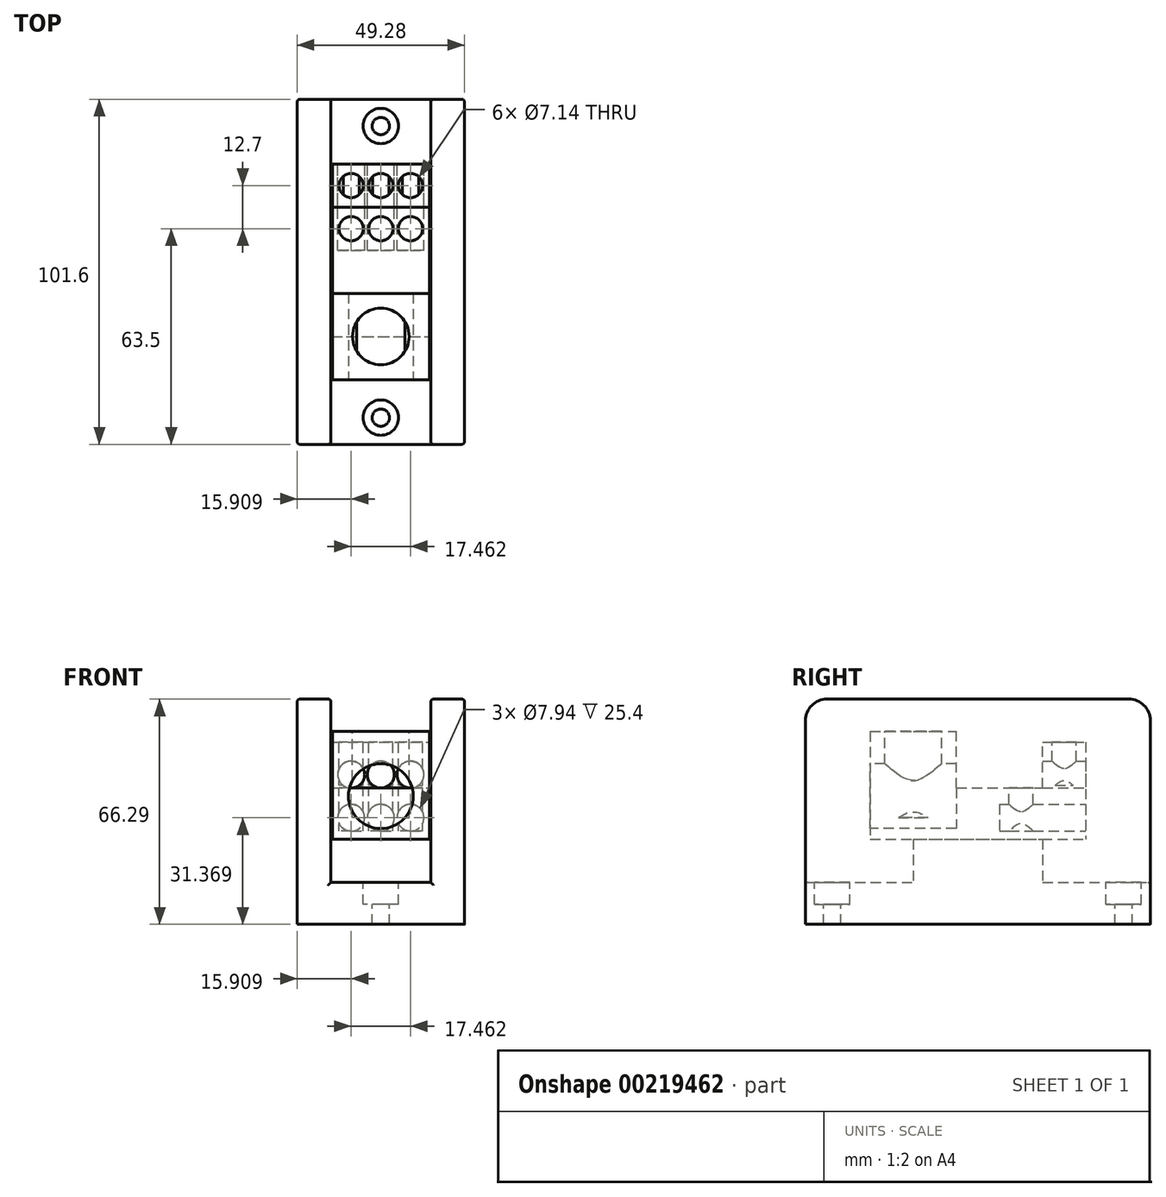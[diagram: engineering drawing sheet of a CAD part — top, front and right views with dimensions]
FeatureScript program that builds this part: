
annotation { "Feature Type Name" : "Feature", "Feature Type Description" : "" }
export const myFeature = defineFeature(function(context is Context, id is Id, definition is map)
    precondition{}
    {
        {
            var Q0;
            Q0=qCreatedBy(makeId("Top.planeOp"),FACE);
            var sketch = newSketch(context, id + "F0", { "sketchPlane" : qUnion([Q0])});
            skLineSegment(sketch, "E0.bottom", {"start": v(-24.64, -50.8) * mm, "end": v(24.64, -50.8) * mm});
            skLineSegment(sketch, "E0.top", {"start": v(-24.64, 50.8) * mm, "end": v(24.64, 50.8) * mm});
            skLineSegment(sketch, "E0.left", {"start": v(-24.64, -50.8) * mm, "end": v(-24.64, 50.8) * mm});
            skLineSegment(sketch, "E0.right", {"start": v(24.64, -50.8) * mm, "end": v(24.64, 50.8) * mm});
            skPoint(sketch, "E0.middle", {"position": v(0, 0) * mm});
            skSolve(sketch);
        }
        {
            var Q0;
            Q0=qSketchRegion(id+"F0",true);
            extrude(context, id + "F1", {"entities" : qUnion([Q0]), "depth" : 66.3 * mm});
        }
        {
            var Q0;
            Q0=makeQuery(id+"F1.opExtrude","CAP_FACE",FACE,{"disambiguationData":[OSD([sQuery(id+"F0.wireOp",EDGE,"E0.bottom"),sQuery(id+"F0.wireOp",EDGE,"E0.top"),sQuery(id+"F0.wireOp",EDGE,"E0.left"),sQuery(id+"F0.wireOp",EDGE,"E0.right")])],"isStart":false});
            var sketch = newSketch(context, id + "F2", { "sketchPlane" : qUnion([Q0])});
            skLineSegment(sketch, "E1.bottom", {"start": v(14.73, -50.8) * mm, "end": v(-14.73, -50.8) * mm});
            skLineSegment(sketch, "E1.top", {"start": v(14.73, 50.8) * mm, "end": v(-14.73, 50.8) * mm});
            skLineSegment(sketch, "E1.left", {"start": v(14.73, -50.8) * mm, "end": v(14.73, 50.8) * mm});
            skLineSegment(sketch, "E1.right", {"start": v(-14.73, -50.8) * mm, "end": v(-14.73, 50.8) * mm});
            skPoint(sketch, "E1.middle", {"position": v(0, 0) * mm});
            skSolve(sketch);
        }
        {
            var Q0;
            Q0=qSketchRegion(id+"F2",true);
            extrude(context, id + "F3", {"entities" : qUnion([Q0]), "operationType" : NewBodyOperationType.REMOVE, "oppositeDirection" : true, "depth" : 53.97 * mm});
        }
        {
            var Q0;
            Q0=makeQuery(id+"F3.boolean.opBoolean","COPY",FACE,{"derivedFrom":makeQuery(id+"F3.opExtrude","CAP_FACE",FACE,{"disambiguationData":[OSD([sQuery(id+"F2.wireOp",EDGE,"E1.bottom"),sQuery(id+"F2.wireOp",EDGE,"E1.top"),sQuery(id+"F2.wireOp",EDGE,"E1.left"),sQuery(id+"F2.wireOp",EDGE,"E1.right")])],"isStart":false})});
            var sketch = newSketch(context, id + "F4", { "sketchPlane" : qUnion([Q0])});
            skPoint(sketch, "E2.middle", {"position": v(0, 42.93) * mm});
            skPoint(sketch, "E3.middle", {"position": v(0, -42.93) * mm});
            skCircle(sketch, "E4", {"center": v(0, 42.93) * mm, "radius": 2.54 * mm});
            skCircle(sketch, "E5", {"center": v(0, -42.93) * mm, "radius": 2.54 * mm});
            skSolve(sketch);
        }
        {
            var Q0;
            Q0=qSketchRegion(id+"F4",true);
            extrude(context, id + "F5", {"entities" : qUnion([Q0]), "operationType" : NewBodyOperationType.REMOVE, "oppositeDirection" : true, "depth" : 12.32 * mm});
        }
        {
            var Q0;
            Q0=makeQuery(id+"F3.boolean.opBoolean","COPY",FACE,{"derivedFrom":makeQuery(id+"F3.opExtrude","CAP_FACE",FACE,{"disambiguationData":[OSD([sQuery(id+"F2.wireOp",EDGE,"E1.bottom"),sQuery(id+"F2.wireOp",EDGE,"E1.top"),sQuery(id+"F2.wireOp",EDGE,"E1.left"),sQuery(id+"F2.wireOp",EDGE,"E1.right")])],"isStart":false})});
            var sketch = newSketch(context, id + "F6", { "sketchPlane" : qUnion([Q0])});
            skCircle(sketch, "E6", {"center": v(0, 42.93) * mm, "radius": 5.2 * mm});
            skCircle(sketch, "E7", {"center": v(0, -42.93) * mm, "radius": 5.2 * mm});
            skSolve(sketch);
        }
        {
            var Q0;
            Q0=qSketchRegion(id+"F6",true);
            extrude(context, id + "F7", {"entities" : qUnion([Q0]), "operationType" : NewBodyOperationType.REMOVE, "oppositeDirection" : true, "depth" : 6.48 * mm});
        }
        {
            var Q0;
            {var subQ0=sQuery(id+"F0.wireOp",EDGE,"E0.left");var subQ1=sQuery(id+"F0.wireOp",EDGE,"E0.top");Q0=makeQuery(id+"F3.boolean.opBoolean","SPLIT",EDGE,{"disambiguationData":[TD([makeQuery(id+"F1.opExtrude","SWEPT_FACE",FACE,{"disambiguationData":[OSD([subQ0])]})])],"derivedFrom":makeQuery(id+"F1.opExtrude","CAP_EDGE",EDGE,{"disambiguationData":[OSD([subQ1])],"isStart":false})});}
            var Q1;
            {var subQ0=sQuery(id+"F0.wireOp",EDGE,"E0.right");var subQ1=sQuery(id+"F0.wireOp",EDGE,"E0.top");Q1=makeQuery(id+"F3.boolean.opBoolean","SPLIT",EDGE,{"disambiguationData":[TD([makeQuery(id+"F1.opExtrude","SWEPT_FACE",FACE,{"disambiguationData":[OSD([subQ0])]})])],"derivedFrom":makeQuery(id+"F1.opExtrude","CAP_EDGE",EDGE,{"disambiguationData":[OSD([subQ1])],"isStart":false})});}
            var Q2;
            {var subQ0=sQuery(id+"F0.wireOp",EDGE,"E0.bottom");var subQ1=sQuery(id+"F0.wireOp",EDGE,"E0.right");Q2=makeQuery(id+"F3.boolean.opBoolean","SPLIT",EDGE,{"disambiguationData":[TD([makeQuery(id+"F1.opExtrude","SWEPT_FACE",FACE,{"disambiguationData":[OSD([subQ1])]})])],"derivedFrom":makeQuery(id+"F1.opExtrude","CAP_EDGE",EDGE,{"disambiguationData":[OSD([subQ0])],"isStart":false})});}
            var Q3;
            {var subQ0=sQuery(id+"F0.wireOp",EDGE,"E0.bottom");var subQ1=sQuery(id+"F0.wireOp",EDGE,"E0.left");Q3=makeQuery(id+"F3.boolean.opBoolean","SPLIT",EDGE,{"disambiguationData":[TD([makeQuery(id+"F1.opExtrude","SWEPT_FACE",FACE,{"disambiguationData":[OSD([subQ1])]})])],"derivedFrom":makeQuery(id+"F1.opExtrude","CAP_EDGE",EDGE,{"disambiguationData":[OSD([subQ0])],"isStart":false})});}
            fillet(context, id + "F8", {"entities" : qUnion([Q0, Q1, Q2, Q3]), "radius" : 6.35 * mm, "tangentPropagation" : true});
        }
        {
            var Q0;
            Q0=makeQuery(id+"F1.opExtrude","SWEPT_EDGE",EDGE,{"disambiguationData":[OSD([sQuery(id+"F0.wireOp",EDGE,"E0.top"),sQuery(id+"F0.wireOp",EDGE,"E0.left")])]});
            var Q1;
            {var subQ0=sQuery(id+"F0.wireOp",EDGE,"E0.left");var subQ1=makeQuery(id+"F1.opExtrude","SWEPT_FACE",FACE,{"disambiguationData":[OSD([subQ0])]});var subQ2=sQuery(id+"F0.wireOp",EDGE,"E0.top");Q1=makeQuery(id+"F8.opFillet","BLEND_EDGE",EDGE,{"blendedFrom":[makeQuery(id+"F3.boolean.opBoolean","SPLIT",EDGE,{"disambiguationData":[TD([subQ1])],"derivedFrom":makeQuery(id+"F1.opExtrude","CAP_EDGE",EDGE,{"disambiguationData":[OSD([subQ2])],"isStart":false})}),subQ1],"blendedInto":[subQ1]});}
            var Q2;
            Q2=makeQuery(id+"F1.opExtrude","CAP_EDGE",EDGE,{"disambiguationData":[OSD([sQuery(id+"F0.wireOp",EDGE,"E0.left")])],"isStart":false});
            var Q3;
            {var subQ0=sQuery(id+"F0.wireOp",EDGE,"E0.left");var subQ1=makeQuery(id+"F1.opExtrude","SWEPT_FACE",FACE,{"disambiguationData":[OSD([subQ0])]});var subQ2=sQuery(id+"F0.wireOp",EDGE,"E0.bottom");Q3=makeQuery(id+"F8.opFillet","BLEND_EDGE",EDGE,{"blendedFrom":[makeQuery(id+"F3.boolean.opBoolean","SPLIT",EDGE,{"disambiguationData":[TD([subQ1])],"derivedFrom":makeQuery(id+"F1.opExtrude","CAP_EDGE",EDGE,{"disambiguationData":[OSD([subQ2])],"isStart":false})}),subQ1],"blendedInto":[subQ1]});}
            var Q4;
            Q4=makeQuery(id+"F1.opExtrude","SWEPT_EDGE",EDGE,{"disambiguationData":[OSD([sQuery(id+"F0.wireOp",EDGE,"E0.bottom"),sQuery(id+"F0.wireOp",EDGE,"E0.left")])]});
            var Q5;
            Q5=makeQuery(id+"F3.boolean.opBoolean","COPY",EDGE,{"derivedFrom":makeQuery(id+"F3.opExtrude","SWEPT_EDGE",EDGE,{"disambiguationData":[OSD([sQuery(id+"F0.wireOp",EDGE,"E0.bottom"),sQuery(id+"F2.wireOp",EDGE,"E1.bottom"),sQuery(id+"F2.wireOp",EDGE,"E1.right")])]})});
            var Q6;
            {var subQ0=makeQuery(id+"F3.opExtrude","SWEPT_FACE",FACE,{"disambiguationData":[OSD([sQuery(id+"F2.wireOp",EDGE,"E1.right")])]});var subQ1=sQuery(id+"F0.wireOp",EDGE,"E0.bottom");var subQ2=sQuery(id+"F0.wireOp",EDGE,"E0.left");Q6=makeQuery(id+"F8.opFillet","BLEND_EDGE",EDGE,{"blendedFrom":[makeQuery(id+"F3.boolean.opBoolean","SPLIT",EDGE,{"disambiguationData":[TD([makeQuery(id+"F1.opExtrude","SWEPT_FACE",FACE,{"disambiguationData":[OSD([subQ2])]})])],"derivedFrom":makeQuery(id+"F1.opExtrude","CAP_EDGE",EDGE,{"disambiguationData":[OSD([subQ1])],"isStart":false})}),makeQuery(id+"F3.boolean.opBoolean","COPY",FACE,{"derivedFrom":subQ0})],"blendedInto":[makeQuery(id+"F3.boolean.opBoolean","COPY",FACE,{"derivedFrom":subQ0})]});}
            var Q7;
            Q7=makeQuery(id+"F3.boolean.opBoolean","COPY",EDGE,{"derivedFrom":makeQuery(id+"F3.opExtrude","CAP_EDGE",EDGE,{"disambiguationData":[OSD([sQuery(id+"F2.wireOp",EDGE,"E1.right")])],"isStart":true})});
            var Q8;
            {var subQ0=makeQuery(id+"F3.opExtrude","SWEPT_FACE",FACE,{"disambiguationData":[OSD([sQuery(id+"F2.wireOp",EDGE,"E1.right")])]});var subQ1=sQuery(id+"F0.wireOp",EDGE,"E0.left");var subQ2=sQuery(id+"F0.wireOp",EDGE,"E0.top");Q8=makeQuery(id+"F8.opFillet","BLEND_EDGE",EDGE,{"blendedFrom":[makeQuery(id+"F3.boolean.opBoolean","SPLIT",EDGE,{"disambiguationData":[TD([makeQuery(id+"F1.opExtrude","SWEPT_FACE",FACE,{"disambiguationData":[OSD([subQ1])]})])],"derivedFrom":makeQuery(id+"F1.opExtrude","CAP_EDGE",EDGE,{"disambiguationData":[OSD([subQ2])],"isStart":false})}),makeQuery(id+"F3.boolean.opBoolean","COPY",FACE,{"derivedFrom":subQ0})],"blendedInto":[makeQuery(id+"F3.boolean.opBoolean","COPY",FACE,{"derivedFrom":subQ0})]});}
            var Q9;
            Q9=makeQuery(id+"F3.boolean.opBoolean","COPY",EDGE,{"derivedFrom":makeQuery(id+"F3.opExtrude","SWEPT_EDGE",EDGE,{"disambiguationData":[OSD([sQuery(id+"F0.wireOp",EDGE,"E0.top"),sQuery(id+"F2.wireOp",EDGE,"E1.top"),sQuery(id+"F2.wireOp",EDGE,"E1.right")])]})});
            var Q10;
            Q10=makeQuery(id+"F1.opExtrude","SWEPT_EDGE",EDGE,{"disambiguationData":[OSD([sQuery(id+"F0.wireOp",EDGE,"E0.top"),sQuery(id+"F0.wireOp",EDGE,"E0.right")])]});
            var Q11;
            {var subQ0=sQuery(id+"F0.wireOp",EDGE,"E0.right");var subQ1=makeQuery(id+"F1.opExtrude","SWEPT_FACE",FACE,{"disambiguationData":[OSD([subQ0])]});var subQ2=sQuery(id+"F0.wireOp",EDGE,"E0.top");Q11=makeQuery(id+"F8.opFillet","BLEND_EDGE",EDGE,{"blendedFrom":[makeQuery(id+"F3.boolean.opBoolean","SPLIT",EDGE,{"disambiguationData":[TD([subQ1])],"derivedFrom":makeQuery(id+"F1.opExtrude","CAP_EDGE",EDGE,{"disambiguationData":[OSD([subQ2])],"isStart":false})}),subQ1],"blendedInto":[subQ1]});}
            var Q12;
            Q12=makeQuery(id+"F1.opExtrude","CAP_EDGE",EDGE,{"disambiguationData":[OSD([sQuery(id+"F0.wireOp",EDGE,"E0.right")])],"isStart":false});
            var Q13;
            {var subQ0=sQuery(id+"F0.wireOp",EDGE,"E0.right");var subQ1=makeQuery(id+"F1.opExtrude","SWEPT_FACE",FACE,{"disambiguationData":[OSD([subQ0])]});var subQ2=sQuery(id+"F0.wireOp",EDGE,"E0.bottom");Q13=makeQuery(id+"F8.opFillet","BLEND_EDGE",EDGE,{"blendedFrom":[makeQuery(id+"F3.boolean.opBoolean","SPLIT",EDGE,{"disambiguationData":[TD([subQ1])],"derivedFrom":makeQuery(id+"F1.opExtrude","CAP_EDGE",EDGE,{"disambiguationData":[OSD([subQ2])],"isStart":false})}),subQ1],"blendedInto":[subQ1]});}
            var Q14;
            Q14=makeQuery(id+"F1.opExtrude","SWEPT_EDGE",EDGE,{"disambiguationData":[OSD([sQuery(id+"F0.wireOp",EDGE,"E0.bottom"),sQuery(id+"F0.wireOp",EDGE,"E0.right")])]});
            var Q15;
            Q15=makeQuery(id+"F3.boolean.opBoolean","COPY",EDGE,{"derivedFrom":makeQuery(id+"F3.opExtrude","SWEPT_EDGE",EDGE,{"disambiguationData":[OSD([sQuery(id+"F0.wireOp",EDGE,"E0.bottom"),sQuery(id+"F2.wireOp",EDGE,"E1.bottom"),sQuery(id+"F2.wireOp",EDGE,"E1.left")])]})});
            var Q16;
            {var subQ0=makeQuery(id+"F3.opExtrude","SWEPT_FACE",FACE,{"disambiguationData":[OSD([sQuery(id+"F2.wireOp",EDGE,"E1.left")])]});var subQ1=sQuery(id+"F0.wireOp",EDGE,"E0.bottom");var subQ2=sQuery(id+"F0.wireOp",EDGE,"E0.right");Q16=makeQuery(id+"F8.opFillet","BLEND_EDGE",EDGE,{"blendedFrom":[makeQuery(id+"F3.boolean.opBoolean","SPLIT",EDGE,{"disambiguationData":[TD([makeQuery(id+"F1.opExtrude","SWEPT_FACE",FACE,{"disambiguationData":[OSD([subQ2])]})])],"derivedFrom":makeQuery(id+"F1.opExtrude","CAP_EDGE",EDGE,{"disambiguationData":[OSD([subQ1])],"isStart":false})}),makeQuery(id+"F3.boolean.opBoolean","COPY",FACE,{"derivedFrom":subQ0})],"blendedInto":[makeQuery(id+"F3.boolean.opBoolean","COPY",FACE,{"derivedFrom":subQ0})]});}
            var Q17;
            Q17=makeQuery(id+"F3.boolean.opBoolean","COPY",EDGE,{"derivedFrom":makeQuery(id+"F3.opExtrude","CAP_EDGE",EDGE,{"disambiguationData":[OSD([sQuery(id+"F2.wireOp",EDGE,"E1.left")])],"isStart":true})});
            var Q18;
            {var subQ0=makeQuery(id+"F3.opExtrude","SWEPT_FACE",FACE,{"disambiguationData":[OSD([sQuery(id+"F2.wireOp",EDGE,"E1.left")])]});var subQ1=sQuery(id+"F0.wireOp",EDGE,"E0.right");var subQ2=sQuery(id+"F0.wireOp",EDGE,"E0.top");Q18=makeQuery(id+"F8.opFillet","BLEND_EDGE",EDGE,{"blendedFrom":[makeQuery(id+"F3.boolean.opBoolean","SPLIT",EDGE,{"disambiguationData":[TD([makeQuery(id+"F1.opExtrude","SWEPT_FACE",FACE,{"disambiguationData":[OSD([subQ1])]})])],"derivedFrom":makeQuery(id+"F1.opExtrude","CAP_EDGE",EDGE,{"disambiguationData":[OSD([subQ2])],"isStart":false})}),makeQuery(id+"F3.boolean.opBoolean","COPY",FACE,{"derivedFrom":subQ0})],"blendedInto":[makeQuery(id+"F3.boolean.opBoolean","COPY",FACE,{"derivedFrom":subQ0})]});}
            var Q19;
            Q19=makeQuery(id+"F3.boolean.opBoolean","COPY",EDGE,{"derivedFrom":makeQuery(id+"F3.opExtrude","SWEPT_EDGE",EDGE,{"disambiguationData":[OSD([sQuery(id+"F0.wireOp",EDGE,"E0.top"),sQuery(id+"F2.wireOp",EDGE,"E1.top"),sQuery(id+"F2.wireOp",EDGE,"E1.left")])]})});
            var Q20;
            Q20=makeQuery(id+"F3.boolean.opBoolean","COPY",EDGE,{"derivedFrom":makeQuery(id+"F3.opExtrude","CAP_EDGE",EDGE,{"disambiguationData":[OSD([sQuery(id+"F2.wireOp",EDGE,"E1.top")])],"isStart":false})});
            var Q21;
            Q21=makeQuery(id+"F3.boolean.opBoolean","COPY",EDGE,{"derivedFrom":makeQuery(id+"F3.opExtrude","CAP_EDGE",EDGE,{"disambiguationData":[OSD([sQuery(id+"F2.wireOp",EDGE,"E1.bottom")])],"isStart":false})});
            fillet(context, id + "F9", {"entities" : qUnion([Q0, Q1, Q2, Q3, Q4, Q5, Q6, Q7, Q8, Q9, Q10, Q11, Q12, Q13, Q14, Q15, Q16, Q17, Q18, Q19, Q20, Q21]), "radius" : 0.81 * mm, "tangentPropagation" : true});
        }
        {
            var Q0;
            Q0=makeQuery(id+"F3.boolean.opBoolean","COPY",FACE,{"derivedFrom":makeQuery(id+"F3.opExtrude","CAP_FACE",FACE,{"disambiguationData":[OSD([sQuery(id+"F2.wireOp",EDGE,"E1.bottom"),sQuery(id+"F2.wireOp",EDGE,"E1.top"),sQuery(id+"F2.wireOp",EDGE,"E1.left"),sQuery(id+"F2.wireOp",EDGE,"E1.right")])],"isStart":false})});
            var sketch = newSketch(context, id + "F10", { "sketchPlane" : qUnion([Q0])});
            skLineSegment(sketch, "E8.bottom", {"start": v(-14.73, -19.05) * mm, "end": v(14.73, -19.05) * mm});
            skLineSegment(sketch, "E8.top", {"start": v(-14.73, 19.05) * mm, "end": v(14.73, 19.05) * mm});
            skLineSegment(sketch, "E8.left", {"start": v(-14.73, -19.05) * mm, "end": v(-14.73, 19.05) * mm});
            skLineSegment(sketch, "E8.right", {"start": v(14.73, -19.05) * mm, "end": v(14.73, 19.05) * mm});
            skPoint(sketch, "E8.middle", {"position": v(0, 0) * mm});
            skSolve(sketch);
        }
        {
            var Q0;
            Q0=qSketchRegion(id+"F10",true);
            extrude(context, id + "F11", {"entities" : qUnion([Q0]), "operationType" : NewBodyOperationType.ADD, "depth" : 12.7 * mm});
        }
        {
            var Q0;
            Q0=makeQuery(id+"F11.opExtrude","CAP_FACE",FACE,{"disambiguationData":[OSD([sQuery(id+"F10.wireOp",EDGE,"E8.bottom"),sQuery(id+"F10.wireOp",EDGE,"E8.top"),sQuery(id+"F10.wireOp",EDGE,"E8.left"),sQuery(id+"F10.wireOp",EDGE,"E8.right")])],"isStart":false});
            var sketch = newSketch(context, id + "F12", { "sketchPlane" : qUnion([Q0])});
            skLineSegment(sketch, "E9.bottom", {"start": v(-14.29, -31.75) * mm, "end": v(14.29, -31.75) * mm});
            skLineSegment(sketch, "E9.top", {"start": v(-14.29, 31.75) * mm, "end": v(14.29, 31.75) * mm});
            skLineSegment(sketch, "E9.left", {"start": v(-14.29, -31.75) * mm, "end": v(-14.29, 31.75) * mm});
            skLineSegment(sketch, "E9.right", {"start": v(14.29, -31.75) * mm, "end": v(14.29, 31.75) * mm});
            skPoint(sketch, "E9.middle", {"position": v(0, 0) * mm});
            skSolve(sketch);
        }
        {
            var Q0;
            Q0=qSketchRegion(id+"F12",true);
            extrude(context, id + "F13", {"entities" : qUnion([Q0]), "depth" : 31.75 * mm});
        }
        {
            var Q0;
            Q0=makeQuery(id+"F13.opExtrude","SWEPT_FACE",FACE,{"disambiguationData":[OSD([sQuery(id+"F12.wireOp",EDGE,"E9.bottom")])]});
            var sketch = newSketch(context, id + "F14", { "sketchPlane" : qUnion([Q0])});
            skCircle(sketch, "E10", {"center": v(0, 37.72) * mm, "radius": 9.53 * mm});
            skSolve(sketch);
        }
        {
            var Q0;
            Q0=qSketchRegion(id+"F14",true);
            extrude(context, id + "F15", {"entities" : qUnion([Q0]), "operationType" : NewBodyOperationType.REMOVE, "oppositeDirection" : true, "depth" : 25.4 * mm});
        }
        {
            var Q0;
            Q0=makeQuery(id+"F13.opExtrude","CAP_FACE",FACE,{"disambiguationData":[OSD([sQuery(id+"F12.wireOp",EDGE,"E9.bottom"),sQuery(id+"F12.wireOp",EDGE,"E9.top"),sQuery(id+"F12.wireOp",EDGE,"E9.left"),sQuery(id+"F12.wireOp",EDGE,"E9.right")])],"isStart":false});
            var sketch = newSketch(context, id + "F16", { "sketchPlane" : qUnion([Q0])});
            skLineSegment(sketch, "E11.bottom", {"start": v(-14.29, 31.75) * mm, "end": v(14.29, 31.75) * mm});
            skLineSegment(sketch, "E11.top", {"start": v(-14.29, 19.05) * mm, "end": v(14.29, 19.05) * mm});
            skLineSegment(sketch, "E11.left", {"start": v(-14.29, 31.75) * mm, "end": v(-14.29, 19.05) * mm});
            skLineSegment(sketch, "E11.right", {"start": v(14.29, 31.75) * mm, "end": v(14.29, 19.05) * mm});
            skSolve(sketch);
        }
        {
            var Q0;
            Q0=makeQuery(id+"F16.imprint","IMPRINT",FACE,{"disambiguationData":[TD([[makeQuery(id+"F16.imprint","IMPRINT",EDGE,{"derivedFrom":sQuery(id+"F16.wireOp",EDGE,"E11.bottom")}),-1.0]])]});
            extrude(context, id + "F17", {"entities" : qUnion([Q0]), "operationType" : NewBodyOperationType.REMOVE, "oppositeDirection" : true, "depth" : 3.17 * mm});
        }
        {
            var Q0;
            Q0=makeQuery(id+"F13.opExtrude","CAP_FACE",FACE,{"disambiguationData":[OSD([sQuery(id+"F12.wireOp",EDGE,"E9.bottom"),sQuery(id+"F12.wireOp",EDGE,"E9.top"),sQuery(id+"F12.wireOp",EDGE,"E9.left"),sQuery(id+"F12.wireOp",EDGE,"E9.right")])],"isStart":false});
            var sketch = newSketch(context, id + "F18", { "sketchPlane" : qUnion([Q0])});
            skLineSegment(sketch, "E12.bottom", {"start": v(-14.29, 19.05) * mm, "end": v(14.29, 19.05) * mm});
            skLineSegment(sketch, "E12.top", {"start": v(-14.29, -6.35) * mm, "end": v(14.29, -6.35) * mm});
            skLineSegment(sketch, "E12.left", {"start": v(-14.29, 19.05) * mm, "end": v(-14.29, -6.35) * mm});
            skLineSegment(sketch, "E12.right", {"start": v(14.29, 19.05) * mm, "end": v(14.29, -6.35) * mm});
            skSolve(sketch);
        }
        {
            var Q0;
            Q0=qSketchRegion(id+"F18",true);
            extrude(context, id + "F19", {"entities" : qUnion([Q0]), "operationType" : NewBodyOperationType.REMOVE, "oppositeDirection" : true, "depth" : 16.67 * mm});
        }
        {
            var Q0;
            Q0=makeQuery(id+"F13.opExtrude","CAP_FACE",FACE,{"disambiguationData":[OSD([sQuery(id+"F12.wireOp",EDGE,"E9.bottom"),sQuery(id+"F12.wireOp",EDGE,"E9.top"),sQuery(id+"F12.wireOp",EDGE,"E9.left"),sQuery(id+"F12.wireOp",EDGE,"E9.right")])],"isStart":false});
            var sketch = newSketch(context, id + "F20", { "sketchPlane" : qUnion([Q0])});
            skCircle(sketch, "E13", {"center": v(0, -19.05) * mm, "radius": 8.33 * mm});
            skSolve(sketch);
        }
        {
            var Q0;
            Q0=qSketchRegion(id+"F20",true);
            extrude(context, id + "F21", {"entities" : qUnion([Q0]), "operationType" : NewBodyOperationType.REMOVE, "oppositeDirection" : true, "depth" : 25.4 * mm});
        }
        {
            var Q0;
            Q0=makeQuery(id+"F17.boolean.opBoolean","COPY",FACE,{"derivedFrom":makeQuery(id+"F17.opExtrude","CAP_FACE",FACE,{"disambiguationData":[OSD([sQuery(id+"F16.wireOp",EDGE,"E11.bottom"),sQuery(id+"F16.wireOp",EDGE,"E11.top"),sQuery(id+"F16.wireOp",EDGE,"E11.left"),sQuery(id+"F16.wireOp",EDGE,"E11.right")])],"isStart":false})});
            var sketch = newSketch(context, id + "F22", { "sketchPlane" : qUnion([Q0])});
            skCircle(sketch, "E14", {"center": v(0, 25.4) * mm, "radius": 3.57 * mm});
            skCircle(sketch, "E15", {"center": v(8.73, 25.4) * mm, "radius": 3.57 * mm});
            skCircle(sketch, "E16", {"center": v(-8.73, 25.4) * mm, "radius": 3.57 * mm});
            skSolve(sketch);
        }
        {
            var Q0;
            Q0=qSketchRegion(id+"F22",true);
            extrude(context, id + "F23", {"entities" : qUnion([Q0]), "operationType" : NewBodyOperationType.REMOVE, "oppositeDirection" : true, "depth" : 12.7 * mm});
        }
        {
            var Q0;
            Q0=makeQuery(id+"F19.boolean.opBoolean","COPY",FACE,{"derivedFrom":makeQuery(id+"F19.opExtrude","CAP_FACE",FACE,{"disambiguationData":[OSD([sQuery(id+"F18.wireOp",EDGE,"E12.bottom"),sQuery(id+"F18.wireOp",EDGE,"E12.top"),sQuery(id+"F18.wireOp",EDGE,"E12.left"),sQuery(id+"F18.wireOp",EDGE,"E12.right")])],"isStart":false})});
            var sketch = newSketch(context, id + "F24", { "sketchPlane" : qUnion([Q0])});
            skCircle(sketch, "E17", {"center": v(0, 12.7) * mm, "radius": 3.57 * mm});
            skCircle(sketch, "E18", {"center": v(8.73, 12.7) * mm, "radius": 3.57 * mm});
            skCircle(sketch, "E19", {"center": v(-8.73, 12.7) * mm, "radius": 3.57 * mm});
            skSolve(sketch);
        }
        {
            var Q0;
            Q0=qSketchRegion(id+"F24",true);
            extrude(context, id + "F25", {"entities" : qUnion([Q0]), "operationType" : NewBodyOperationType.REMOVE, "oppositeDirection" : true, "depth" : 12.7 * mm});
        }
        {
            var Q0;
            Q0=makeQuery(id+"F13.opExtrude","SWEPT_FACE",FACE,{"disambiguationData":[OSD([sQuery(id+"F12.wireOp",EDGE,"E9.top")])]});
            var sketch = newSketch(context, id + "F26", { "sketchPlane" : qUnion([Q0])});
            skCircle(sketch, "E20", {"center": v(0, 31.37) * mm, "radius": 3.97 * mm});
            skCircle(sketch, "E21", {"center": v(0, 44.07) * mm, "radius": 3.97 * mm});
            skCircle(sketch, "E22", {"center": v(-8.73, 31.37) * mm, "radius": 3.97 * mm});
            skCircle(sketch, "E23", {"center": v(8.73, 31.37) * mm, "radius": 3.97 * mm});
            skCircle(sketch, "E24", {"center": v(8.73, 44.07) * mm, "radius": 3.97 * mm});
            skCircle(sketch, "E25", {"center": v(-8.73, 44.07) * mm, "radius": 3.97 * mm});
            skSolve(sketch);
        }
        {
            var Q0;
            Q0=qSketchRegion(id+"F26",true);
            extrude(context, id + "F27", {"entities" : qUnion([Q0]), "operationType" : NewBodyOperationType.REMOVE, "oppositeDirection" : true, "depth" : 25.4 * mm});
        }
    });
